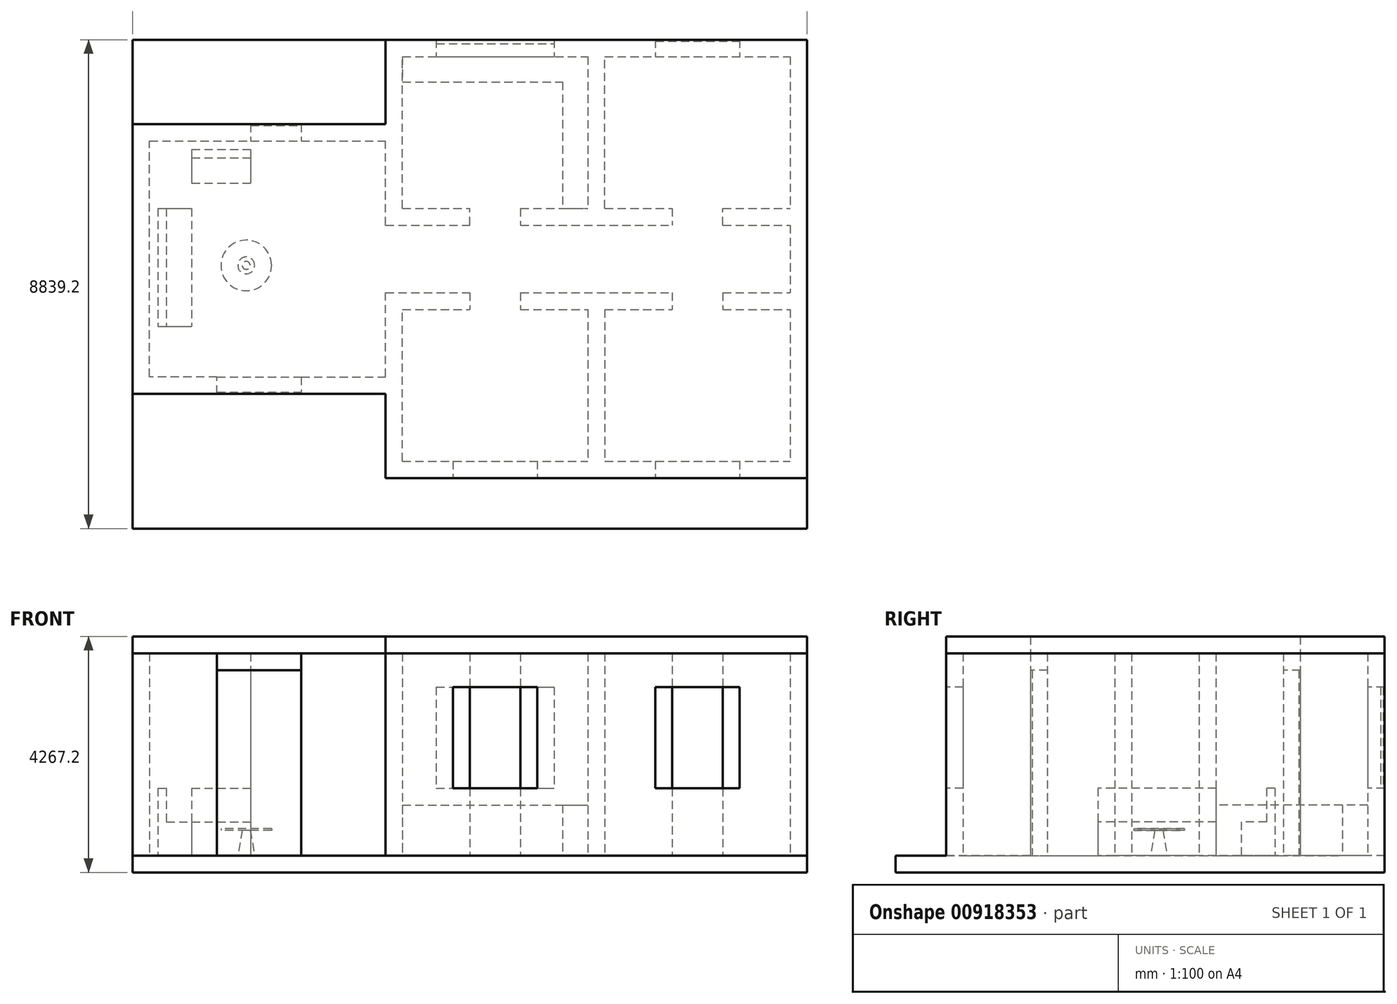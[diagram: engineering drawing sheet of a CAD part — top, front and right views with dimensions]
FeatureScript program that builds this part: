
annotation { "Feature Type Name" : "Feature", "Feature Type Description" : "" }
export const myFeature = defineFeature(function(context is Context, id is Id, definition is map)
    precondition{}
    {
        {
            var Q0;
            Q0=qCreatedBy(makeId("Top.planeOp"),FACE);
            var sketch = newSketch(context, id + "F0", { "sketchPlane" : qUnion([Q0])});
            skLineSegment(sketch, "E0", {"start": v(-1524, -1642.32) * mm, "end": v(0, -1642.32) * mm});
            skLineSegment(sketch, "E1", {"start": v(0, -1642.32) * mm, "end": v(0, -1337.52) * mm});
            skLineSegment(sketch, "E2", {"start": v(0, -1337.52) * mm, "end": v(-1524, -1337.52) * mm});
            skLineSegment(sketch, "E3", {"start": v(-1524, -1337.52) * mm, "end": v(-1524, -1642.32) * mm});
            skLineSegment(sketch, "E4.bottom", {"start": v(1524, -1337.52) * mm, "end": v(3048, -1337.52) * mm});
            skLineSegment(sketch, "E4.top", {"start": v(1524, -1642.32) * mm, "end": v(3048, -1642.32) * mm});
            skLineSegment(sketch, "E4.left", {"start": v(1524, -1337.52) * mm, "end": v(1524, -1642.32) * mm});
            skLineSegment(sketch, "E4.right", {"start": v(3048, -1337.52) * mm, "end": v(3048, -1642.32) * mm});
            skLineSegment(sketch, "E5.bottom", {"start": v(-1524, -1337.52) * mm, "end": v(-1219.2, -1337.52) * mm});
            skLineSegment(sketch, "E5.top", {"start": v(-1524, 3234.48) * mm, "end": v(-1219.2, 3234.48) * mm});
            skLineSegment(sketch, "E5.left", {"start": v(-1524, -1337.52) * mm, "end": v(-1524, 3234.48) * mm});
            skLineSegment(sketch, "E5.right", {"start": v(-1219.2, -1337.52) * mm, "end": v(-1219.2, 3234.48) * mm});
            skLineSegment(sketch, "E6.bottom", {"start": v(-1219.2, 3234.48) * mm, "end": v(609.6, 3234.48) * mm});
            skLineSegment(sketch, "E6.top", {"start": v(-1219.2, 2929.68) * mm, "end": v(609.6, 2929.68) * mm});
            skLineSegment(sketch, "E6.left", {"start": v(-1219.2, 3234.48) * mm, "end": v(-1219.2, 2929.68) * mm});
            skLineSegment(sketch, "E6.right", {"start": v(609.6, 3234.48) * mm, "end": v(609.6, 2929.68) * mm});
            skLineSegment(sketch, "E7.bottom", {"start": v(1524, 3234.48) * mm, "end": v(3048, 3234.48) * mm});
            skLineSegment(sketch, "E7.top", {"start": v(1524, 2929.68) * mm, "end": v(3048, 2929.68) * mm});
            skLineSegment(sketch, "E7.left", {"start": v(1524, 3234.48) * mm, "end": v(1524, 2929.68) * mm});
            skLineSegment(sketch, "E7.right", {"start": v(3048, 3234.48) * mm, "end": v(3048, 2929.68) * mm});
            skLineSegment(sketch, "E8.bottom", {"start": v(3048, -3166.32) * mm, "end": v(3352.8, -3166.32) * mm});
            skLineSegment(sketch, "E8.top", {"start": v(3048, 186.48) * mm, "end": v(3352.8, 186.48) * mm});
            skLineSegment(sketch, "E8.left", {"start": v(3048, -3166.32) * mm, "end": v(3048, 186.48) * mm});
            skLineSegment(sketch, "E8.right", {"start": v(3352.8, -3166.32) * mm, "end": v(3352.8, 186.48) * mm});
            skLineSegment(sketch, "E9.bottom", {"start": v(3352.8, 1405.68) * mm, "end": v(3048, 1405.68) * mm});
            skLineSegment(sketch, "E9.top", {"start": v(3352.8, 4758.48) * mm, "end": v(3048, 4758.48) * mm});
            skLineSegment(sketch, "E9.left", {"start": v(3352.8, 1405.68) * mm, "end": v(3352.8, 4758.48) * mm});
            skLineSegment(sketch, "E9.right", {"start": v(3048, 1405.68) * mm, "end": v(3048, 4758.48) * mm});
            skLineSegment(sketch, "E10.bottom", {"start": v(3352.8, 1405.68) * mm, "end": v(4572, 1405.68) * mm});
            skLineSegment(sketch, "E10.top", {"start": v(3352.8, 1710.48) * mm, "end": v(4572, 1710.48) * mm});
            skLineSegment(sketch, "E10.left", {"start": v(3352.8, 1405.68) * mm, "end": v(3352.8, 1710.48) * mm});
            skLineSegment(sketch, "E10.right", {"start": v(4572, 1405.68) * mm, "end": v(4572, 1710.48) * mm});
            skLineSegment(sketch, "E11.bottom", {"start": v(5486.4, 1710.48) * mm, "end": v(6705.6, 1710.48) * mm});
            skLineSegment(sketch, "E11.top", {"start": v(5486.4, 1405.68) * mm, "end": v(6705.6, 1405.68) * mm});
            skLineSegment(sketch, "E11.left", {"start": v(5486.4, 1710.48) * mm, "end": v(5486.4, 1405.68) * mm});
            skLineSegment(sketch, "E11.right", {"start": v(6705.6, 1710.48) * mm, "end": v(6705.6, 1405.68) * mm});
            skLineSegment(sketch, "E12.bottom", {"start": v(6705.6, 1405.68) * mm, "end": v(7010.4, 1405.68) * mm});
            skLineSegment(sketch, "E12.top", {"start": v(6705.6, 4758.48) * mm, "end": v(7010.4, 4758.48) * mm});
            skLineSegment(sketch, "E12.left", {"start": v(6705.6, 1405.68) * mm, "end": v(6705.6, 4758.48) * mm});
            skLineSegment(sketch, "E12.right", {"start": v(7010.4, 1405.68) * mm, "end": v(7010.4, 4758.48) * mm});
            skLineSegment(sketch, "E13.bottom", {"start": v(3352.8, 4758.48) * mm, "end": v(3962.4, 4758.48) * mm});
            skLineSegment(sketch, "E13.top", {"start": v(3352.8, 4453.68) * mm, "end": v(3962.4, 4453.68) * mm});
            skLineSegment(sketch, "E13.left", {"start": v(3352.8, 4758.48) * mm, "end": v(3352.8, 4453.68) * mm});
            skLineSegment(sketch, "E13.right", {"start": v(3962.4, 4758.48) * mm, "end": v(3962.4, 4453.68) * mm});
            skLineSegment(sketch, "E14.bottom", {"start": v(6096, 4758.48) * mm, "end": v(6705.6, 4758.48) * mm});
            skLineSegment(sketch, "E14.top", {"start": v(6096, 4453.68) * mm, "end": v(6705.6, 4453.68) * mm});
            skLineSegment(sketch, "E14.left", {"start": v(6096, 4758.48) * mm, "end": v(6096, 4453.68) * mm});
            skLineSegment(sketch, "E14.right", {"start": v(6705.6, 4758.48) * mm, "end": v(6705.6, 4453.68) * mm});
            skLineSegment(sketch, "E15.bottom", {"start": v(3352.8, 186.48) * mm, "end": v(4572, 186.48) * mm});
            skLineSegment(sketch, "E15.top", {"start": v(3352.8, -118.32) * mm, "end": v(4572, -118.32) * mm});
            skLineSegment(sketch, "E15.left", {"start": v(3352.8, 186.48) * mm, "end": v(3352.8, -118.32) * mm});
            skLineSegment(sketch, "E15.right", {"start": v(4572, 186.48) * mm, "end": v(4572, -118.32) * mm});
            skLineSegment(sketch, "E16.bottom", {"start": v(5486.4, 186.48) * mm, "end": v(6705.6, 186.48) * mm});
            skLineSegment(sketch, "E16.top", {"start": v(5486.4, -118.32) * mm, "end": v(6705.6, -118.32) * mm});
            skLineSegment(sketch, "E16.left", {"start": v(5486.4, 186.48) * mm, "end": v(5486.4, -118.32) * mm});
            skLineSegment(sketch, "E16.right", {"start": v(6705.6, 186.48) * mm, "end": v(6705.6, -118.32) * mm});
            skLineSegment(sketch, "E17.bottom", {"start": v(6705.6, 186.48) * mm, "end": v(7010.4, 186.48) * mm});
            skLineSegment(sketch, "E17.top", {"start": v(6705.6, -3166.32) * mm, "end": v(7010.4, -3166.32) * mm});
            skLineSegment(sketch, "E17.left", {"start": v(6705.6, 186.48) * mm, "end": v(6705.6, -3166.32) * mm});
            skLineSegment(sketch, "E17.right", {"start": v(7010.4, 186.48) * mm, "end": v(7010.4, -3166.32) * mm});
            skLineSegment(sketch, "E18.left", {"start": v(3352.8, -3166.32) * mm, "end": v(3352.8, -2861.52) * mm});
            skLineSegment(sketch, "E19.left", {"start": v(6705.6, -3166.32) * mm, "end": v(6705.6, -2861.52) * mm});
            skLineSegment(sketch, "E20.bottom", {"start": v(7010.4, 4758.48) * mm, "end": v(7924.8, 4758.48) * mm});
            skLineSegment(sketch, "E20.top", {"start": v(7010.4, 4453.68) * mm, "end": v(7924.8, 4453.68) * mm});
            skLineSegment(sketch, "E20.left", {"start": v(7010.4, 4758.48) * mm, "end": v(7010.4, 4453.68) * mm});
            skLineSegment(sketch, "E20.right", {"start": v(7924.8, 4758.48) * mm, "end": v(7924.8, 4453.68) * mm});
            skLineSegment(sketch, "E21.bottom", {"start": v(9448.8, 4758.48) * mm, "end": v(10363.2, 4758.48) * mm});
            skLineSegment(sketch, "E21.top", {"start": v(9448.8, 4453.68) * mm, "end": v(10363.2, 4453.68) * mm});
            skLineSegment(sketch, "E21.left", {"start": v(9448.8, 4758.48) * mm, "end": v(9448.8, 4453.68) * mm});
            skLineSegment(sketch, "E21.right", {"start": v(10363.2, 4758.48) * mm, "end": v(10363.2, 4453.68) * mm});
            skLineSegment(sketch, "E22.bottom", {"start": v(10363.2, 4758.48) * mm, "end": v(10668, 4758.48) * mm});
            skLineSegment(sketch, "E22.top", {"start": v(10363.2, 1405.68) * mm, "end": v(10668, 1405.68) * mm});
            skLineSegment(sketch, "E22.left", {"start": v(10363.2, 4758.48) * mm, "end": v(10363.2, 1405.68) * mm});
            skLineSegment(sketch, "E22.right", {"start": v(10668, 4758.48) * mm, "end": v(10668, 1405.68) * mm});
            skPoint(sketch, "E23.oppositeSnap0", {"position": v(6858, 1405.68) * mm});
            skLineSegment(sketch, "E23.bottom", {"start": v(7010.4, 1710.48) * mm, "end": v(8229.6, 1710.48) * mm});
            skLineSegment(sketch, "E23.top", {"start": v(7010.4, 1405.68) * mm, "end": v(8229.6, 1405.68) * mm});
            skLineSegment(sketch, "E23.left", {"start": v(7010.4, 1710.48) * mm, "end": v(7010.4, 1405.68) * mm});
            skLineSegment(sketch, "E23.right", {"start": v(8229.6, 1710.48) * mm, "end": v(8229.6, 1405.68) * mm});
            skLineSegment(sketch, "E24.bottom", {"start": v(9144, 1405.68) * mm, "end": v(10363.2, 1405.68) * mm});
            skLineSegment(sketch, "E24.top", {"start": v(9144, 1710.48) * mm, "end": v(10363.2, 1710.48) * mm});
            skLineSegment(sketch, "E24.left", {"start": v(9144, 1405.68) * mm, "end": v(9144, 1710.48) * mm});
            skLineSegment(sketch, "E24.right", {"start": v(10363.2, 1405.68) * mm, "end": v(10363.2, 1710.48) * mm});
            skLineSegment(sketch, "E25.bottom", {"start": v(7010.4, 186.48) * mm, "end": v(8229.6, 186.48) * mm});
            skLineSegment(sketch, "E25.top", {"start": v(7010.4, -118.32) * mm, "end": v(8229.6, -118.32) * mm});
            skLineSegment(sketch, "E25.left", {"start": v(7010.4, 186.48) * mm, "end": v(7010.4, -118.32) * mm});
            skLineSegment(sketch, "E25.right", {"start": v(8229.6, 186.48) * mm, "end": v(8229.6, -118.32) * mm});
            skLineSegment(sketch, "E26.bottom", {"start": v(9144, 186.48) * mm, "end": v(10363.2, 186.48) * mm});
            skLineSegment(sketch, "E26.top", {"start": v(9144, -118.32) * mm, "end": v(10363.2, -118.32) * mm});
            skLineSegment(sketch, "E26.left", {"start": v(9144, 186.48) * mm, "end": v(9144, -118.32) * mm});
            skLineSegment(sketch, "E26.right", {"start": v(10363.2, 186.48) * mm, "end": v(10363.2, -118.32) * mm});
            skLineSegment(sketch, "E27.bottom", {"start": v(7010.4, -3166.32) * mm, "end": v(7924.8, -3166.32) * mm});
            skLineSegment(sketch, "E27.top", {"start": v(7010.4, -2861.52) * mm, "end": v(7924.8, -2861.52) * mm});
            skLineSegment(sketch, "E27.left", {"start": v(7010.4, -3166.32) * mm, "end": v(7010.4, -2861.52) * mm});
            skLineSegment(sketch, "E27.right", {"start": v(7924.8, -3166.32) * mm, "end": v(7924.8, -2861.52) * mm});
            skLineSegment(sketch, "E28.bottom", {"start": v(9448.8, -2861.52) * mm, "end": v(10363.2, -2861.52) * mm});
            skLineSegment(sketch, "E28.top", {"start": v(9448.8, -3166.32) * mm, "end": v(10363.2, -3166.32) * mm});
            skLineSegment(sketch, "E28.left", {"start": v(9448.8, -2861.52) * mm, "end": v(9448.8, -3166.32) * mm});
            skLineSegment(sketch, "E28.right", {"start": v(10363.2, -2861.52) * mm, "end": v(10363.2, -3166.32) * mm});
            skLineSegment(sketch, "E29.top", {"start": v(10363.2, -3166.32) * mm, "end": v(10668, -3166.32) * mm});
            skLineSegment(sketch, "E29.left", {"start": v(10363.2, 1405.68) * mm, "end": v(10363.2, -3166.32) * mm});
            skLineSegment(sketch, "E29.right", {"start": v(10668, 1405.68) * mm, "end": v(10668, -3166.32) * mm});
            skLineSegment(sketch, "E30.bottom", {"start": v(3352.8, -2861.52) * mm, "end": v(4267.2, -2861.52) * mm});
            skLineSegment(sketch, "E30.top", {"start": v(3352.8, -3166.32) * mm, "end": v(4267.2, -3166.32) * mm});
            skLineSegment(sketch, "E30.left", {"start": v(3352.8, -2861.52) * mm, "end": v(3352.8, -3166.32) * mm});
            skLineSegment(sketch, "E30.right", {"start": v(4267.2, -2861.52) * mm, "end": v(4267.2, -3166.32) * mm});
            skLineSegment(sketch, "E31.bottom", {"start": v(6705.6, -2861.52) * mm, "end": v(5791.2, -2861.52) * mm});
            skLineSegment(sketch, "E31.top", {"start": v(6705.6, -3166.32) * mm, "end": v(5791.2, -3166.32) * mm});
            skLineSegment(sketch, "E31.left", {"start": v(6705.6, -2861.52) * mm, "end": v(6705.6, -3166.32) * mm});
            skLineSegment(sketch, "E31.right", {"start": v(5791.2, -2861.52) * mm, "end": v(5791.2, -3166.32) * mm});
            skSolve(sketch);
        }
        {
            var Q0;
            Q0=qSketchRegion(id+"F0",true);
            extrude(context, id + "F1", {"entities" : qUnion([Q0]), "depth" : 3657.6 * mm});
        }
        {
            var Q0;
            Q0=qCreatedBy(makeId("Top.planeOp"),FACE);
            var sketch = newSketch(context, id + "F2", { "sketchPlane" : qUnion([Q0])});
            skLineSegment(sketch, "E32.bottom", {"start": v(-1524, 4758.48) * mm, "end": v(10668, 4758.48) * mm});
            skLineSegment(sketch, "E32.top", {"start": v(-1524, -3166.32) * mm, "end": v(10668, -3166.32) * mm});
            skLineSegment(sketch, "E32.left", {"start": v(-1524, 4758.48) * mm, "end": v(-1524, -3166.32) * mm});
            skLineSegment(sketch, "E32.right", {"start": v(10668, 4758.48) * mm, "end": v(10668, -3166.32) * mm});
            skLineSegment(sketch, "E33.top", {"start": v(-1524, -4080.72) * mm, "end": v(10668, -4080.72) * mm});
            skLineSegment(sketch, "E33.left", {"start": v(-1524, -3166.32) * mm, "end": v(-1524, -4080.72) * mm});
            skLineSegment(sketch, "E33.right", {"start": v(10668, -3166.32) * mm, "end": v(10668, -4080.72) * mm});
            skSolve(sketch);
        }
        {
            var Q0;
            Q0=qSketchRegion(id+"F2",true);
            extrude(context, id + "F3", {"entities" : qUnion([Q0]), "oppositeDirection" : true, "depth" : 304.8 * mm});
        }
        {
            var Q0;
            Q0=qCreatedBy(makeId("Top.planeOp"),FACE);
            var sketch = newSketch(context, id + "F4", { "sketchPlane" : qUnion([Q0])});
            skLineSegment(sketch, "E34.bottom", {"start": v(3962.4, 4758.48) * mm, "end": v(6096, 4758.48) * mm});
            skLineSegment(sketch, "E34.top", {"start": v(3962.4, 4453.68) * mm, "end": v(6096, 4453.68) * mm});
            skLineSegment(sketch, "E34.left", {"start": v(3962.4, 4758.48) * mm, "end": v(3962.4, 4453.68) * mm});
            skLineSegment(sketch, "E34.right", {"start": v(6096, 4758.48) * mm, "end": v(6096, 4453.68) * mm});
            skLineSegment(sketch, "E35.bottom", {"start": v(7924.8, -2861.52) * mm, "end": v(9448.8, -2861.52) * mm});
            skLineSegment(sketch, "E35.top", {"start": v(7924.8, -3166.32) * mm, "end": v(9448.8, -3166.32) * mm});
            skLineSegment(sketch, "E35.left", {"start": v(7924.8, -2861.52) * mm, "end": v(7924.8, -3166.32) * mm});
            skLineSegment(sketch, "E35.right", {"start": v(9448.8, -2861.52) * mm, "end": v(9448.8, -3166.32) * mm});
            skLineSegment(sketch, "E36.bottom", {"start": v(4267.2, -2861.52) * mm, "end": v(5791.2, -2861.52) * mm});
            skLineSegment(sketch, "E36.top", {"start": v(4267.2, -3166.32) * mm, "end": v(5791.2, -3166.32) * mm});
            skLineSegment(sketch, "E36.left", {"start": v(4267.2, -2861.52) * mm, "end": v(4267.2, -3166.32) * mm});
            skLineSegment(sketch, "E36.right", {"start": v(5791.2, -2861.52) * mm, "end": v(5791.2, -3166.32) * mm});
            skSolve(sketch);
        }
        {
            var Q0;
            Q0=qSketchRegion(id+"F4",true);
            extrude(context, id + "F5", {"entities" : qUnion([Q0]), "depth" : 1219.2 * mm});
        }
        {
            var Q0;
            Q0=qCreatedBy(makeId("Top.planeOp"),FACE);
            cPlane(context, id + "F6", {"entities" : qUnion([Q0]), "cplaneType" : CPlaneType.OFFSET, "offset" : 3048 * mm, "width" : 152.4 * mm, "height" : 152.4 * mm});
        }
        {
            var Q0;
            Q0=qCreatedBy(id+"F6.planeOp",FACE);
            var sketch = newSketch(context, id + "F7", { "sketchPlane" : qUnion([Q0])});
            skLineSegment(sketch, "E37.bottom", {"start": v(3962.4, 4758.48) * mm, "end": v(6096, 4758.48) * mm});
            skLineSegment(sketch, "E37.top", {"start": v(3962.4, 4453.68) * mm, "end": v(6096, 4453.68) * mm});
            skLineSegment(sketch, "E37.left", {"start": v(3962.4, 4758.48) * mm, "end": v(3962.4, 4453.68) * mm});
            skLineSegment(sketch, "E37.right", {"start": v(6096, 4758.48) * mm, "end": v(6096, 4453.68) * mm});
            skLineSegment(sketch, "E38.bottom", {"start": v(7924.8, 4758.48) * mm, "end": v(9448.8, 4758.48) * mm});
            skLineSegment(sketch, "E38.top", {"start": v(7924.8, 4453.68) * mm, "end": v(9448.8, 4453.68) * mm});
            skLineSegment(sketch, "E38.left", {"start": v(7924.8, 4758.48) * mm, "end": v(7924.8, 4453.68) * mm});
            skLineSegment(sketch, "E38.right", {"start": v(9448.8, 4758.48) * mm, "end": v(9448.8, 4453.68) * mm});
            skLineSegment(sketch, "E39.bottom", {"start": v(7924.8, -2861.52) * mm, "end": v(9448.8, -2861.52) * mm});
            skLineSegment(sketch, "E39.top", {"start": v(7924.8, -3166.32) * mm, "end": v(9448.8, -3166.32) * mm});
            skLineSegment(sketch, "E39.left", {"start": v(7924.8, -2861.52) * mm, "end": v(7924.8, -3166.32) * mm});
            skLineSegment(sketch, "E39.right", {"start": v(9448.8, -2861.52) * mm, "end": v(9448.8, -3166.32) * mm});
            skLineSegment(sketch, "E40.bottom", {"start": v(4267.2, -2861.52) * mm, "end": v(5791.2, -2861.52) * mm});
            skLineSegment(sketch, "E40.top", {"start": v(4267.2, -3166.32) * mm, "end": v(5791.2, -3166.32) * mm});
            skLineSegment(sketch, "E40.left", {"start": v(4267.2, -2861.52) * mm, "end": v(4267.2, -3166.32) * mm});
            skLineSegment(sketch, "E40.right", {"start": v(5791.2, -2861.52) * mm, "end": v(5791.2, -3166.32) * mm});
            skSolve(sketch);
        }
        {
            var Q0;
            Q0=qSketchRegion(id+"F7",true);
            var Q1;
            Q1=makeQuery(id+"F1.opExtrude","CAP_FACE",FACE,{"disambiguationData":[OSD([sQuery(id+"F0.wireOp",EDGE,"E4.bottom"),sQuery(id+"F0.wireOp",EDGE,"E4.top"),sQuery(id+"F0.wireOp",EDGE,"E4.left"),sQuery(id+"F0.wireOp",EDGE,"E8.bottom"),sQuery(id+"F0.wireOp",EDGE,"E8.top"),sQuery(id+"F0.wireOp",EDGE,"E8.left"),sQuery(id+"F0.wireOp",EDGE,"E8.right"),sQuery(id+"F0.wireOp",EDGE,"E15.bottom"),sQuery(id+"F0.wireOp",EDGE,"E15.top"),sQuery(id+"F0.wireOp",EDGE,"E15.right"),sQuery(id+"F0.wireOp",EDGE,"E18.bottom"),sQuery(id+"F0.wireOp",EDGE,"E18.top"),sQuery(id+"F0.wireOp",EDGE,"E18.right")])],"isStart":false});
            extrude(context, id + "F8", {"entities" : qUnion([Q0]), "depth" : 609.6 * mm});
        }
        {
            var Q0;
            Q0=qCreatedBy(makeId("Top.planeOp"),FACE);
            cPlane(context, id + "F9", {"entities" : qUnion([Q0]), "cplaneType" : CPlaneType.OFFSET, "offset" : 3657.6 * mm, "width" : 152.4 * mm, "height" : 152.4 * mm});
        }
        {
            var Q0;
            Q0=qCreatedBy(id+"F9.planeOp",FACE);
            var sketch = newSketch(context, id + "F10", { "sketchPlane" : qUnion([Q0])});
            skLineSegment(sketch, "E41", {"start": v(-1524, 3234.48) * mm, "end": v(-1524, -1642.32) * mm});
            skLineSegment(sketch, "E42", {"start": v(-1524, -1642.32) * mm, "end": v(3048, -1642.32) * mm});
            skLineSegment(sketch, "E43", {"start": v(3048, -1642.32) * mm, "end": v(3048, -3166.32) * mm});
            skLineSegment(sketch, "E44", {"start": v(3048, -3166.32) * mm, "end": v(10668, -3166.32) * mm});
            skLineSegment(sketch, "E45", {"start": v(10668, -3166.32) * mm, "end": v(10668, 4758.48) * mm});
            skLineSegment(sketch, "E46", {"start": v(10668, 4758.48) * mm, "end": v(3048, 4758.48) * mm});
            skLineSegment(sketch, "E47", {"start": v(3048, 4758.48) * mm, "end": v(3048, 3234.48) * mm});
            skLineSegment(sketch, "E48", {"start": v(3048, 3234.48) * mm, "end": v(-1524, 3234.48) * mm});
            skSolve(sketch);
        }
        {
            var Q0;
            Q0=qSketchRegion(id+"F10",true);
            extrude(context, id + "F11", {"entities" : qUnion([Q0]), "depth" : 304.8 * mm});
        }
        {
            var Q0;
            Q0=makeQuery(id+"F1.opExtrude","SWEPT_BODY",BODY,{"disambiguationData":[OSD([sQuery(id+"F0.wireOp",EDGE,"E0"),sQuery(id+"F0.wireOp",EDGE,"E1"),sQuery(id+"F0.wireOp",EDGE,"E2"),sQuery(id+"F0.wireOp",EDGE,"E3"),sQuery(id+"F0.wireOp",EDGE,"E5.top"),sQuery(id+"F0.wireOp",EDGE,"E5.left"),sQuery(id+"F0.wireOp",EDGE,"E5.right"),sQuery(id+"F0.wireOp",EDGE,"E6.bottom"),sQuery(id+"F0.wireOp",EDGE,"E6.top"),sQuery(id+"F0.wireOp",EDGE,"E6.right")])]});
            var Q1;
            Q1=makeQuery(id+"F1.opExtrude","SWEPT_BODY",BODY,{"disambiguationData":[OSD([sQuery(id+"F0.wireOp",EDGE,"E4.bottom"),sQuery(id+"F0.wireOp",EDGE,"E4.top"),sQuery(id+"F0.wireOp",EDGE,"E4.left"),sQuery(id+"F0.wireOp",EDGE,"E8.bottom"),sQuery(id+"F0.wireOp",EDGE,"E8.top"),sQuery(id+"F0.wireOp",EDGE,"E8.left"),sQuery(id+"F0.wireOp",EDGE,"E8.right"),sQuery(id+"F0.wireOp",EDGE,"E15.bottom"),sQuery(id+"F0.wireOp",EDGE,"E15.top"),sQuery(id+"F0.wireOp",EDGE,"E15.right"),sQuery(id+"F0.wireOp",EDGE,"E18.bottom"),sQuery(id+"F0.wireOp",EDGE,"E18.top"),sQuery(id+"F0.wireOp",EDGE,"E18.right")])]});
            var Q2;
            Q2=makeQuery(id+"F1.opExtrude","SWEPT_BODY",BODY,{"disambiguationData":[OSD([sQuery(id+"F0.wireOp",EDGE,"E7.bottom"),sQuery(id+"F0.wireOp",EDGE,"E7.top"),sQuery(id+"F0.wireOp",EDGE,"E7.left"),sQuery(id+"F0.wireOp",EDGE,"E9.bottom"),sQuery(id+"F0.wireOp",EDGE,"E9.top"),sQuery(id+"F0.wireOp",EDGE,"E9.left"),sQuery(id+"F0.wireOp",EDGE,"E9.right"),sQuery(id+"F0.wireOp",EDGE,"E10.bottom"),sQuery(id+"F0.wireOp",EDGE,"E10.top"),sQuery(id+"F0.wireOp",EDGE,"E10.right"),sQuery(id+"F0.wireOp",EDGE,"E13.bottom"),sQuery(id+"F0.wireOp",EDGE,"E13.top"),sQuery(id+"F0.wireOp",EDGE,"E13.right")])]});
            var Q3;
            Q3=makeQuery(id+"F1.opExtrude","SWEPT_BODY",BODY,{"disambiguationData":[OSD([sQuery(id+"F0.wireOp",EDGE,"E11.bottom"),sQuery(id+"F0.wireOp",EDGE,"E11.top"),sQuery(id+"F0.wireOp",EDGE,"E11.left"),sQuery(id+"F0.wireOp",EDGE,"E12.bottom"),sQuery(id+"F0.wireOp",EDGE,"E12.top"),sQuery(id+"F0.wireOp",EDGE,"E12.left"),sQuery(id+"F0.wireOp",EDGE,"E12.right"),sQuery(id+"F0.wireOp",EDGE,"E14.bottom"),sQuery(id+"F0.wireOp",EDGE,"E14.top"),sQuery(id+"F0.wireOp",EDGE,"E14.left"),sQuery(id+"F0.wireOp",EDGE,"E20.bottom"),sQuery(id+"F0.wireOp",EDGE,"E20.top"),sQuery(id+"F0.wireOp",EDGE,"E20.right"),sQuery(id+"F0.wireOp",EDGE,"E23.bottom"),sQuery(id+"F0.wireOp",EDGE,"E23.top"),sQuery(id+"F0.wireOp",EDGE,"E23.right")])]});
            var Q4;
            Q4=makeQuery(id+"F1.opExtrude","SWEPT_BODY",BODY,{"disambiguationData":[OSD([sQuery(id+"F0.wireOp",EDGE,"E16.bottom"),sQuery(id+"F0.wireOp",EDGE,"E16.top"),sQuery(id+"F0.wireOp",EDGE,"E16.left"),sQuery(id+"F0.wireOp",EDGE,"E17.bottom"),sQuery(id+"F0.wireOp",EDGE,"E17.top"),sQuery(id+"F0.wireOp",EDGE,"E17.left"),sQuery(id+"F0.wireOp",EDGE,"E17.right"),sQuery(id+"F0.wireOp",EDGE,"E19.bottom"),sQuery(id+"F0.wireOp",EDGE,"E19.top"),sQuery(id+"F0.wireOp",EDGE,"E19.right"),sQuery(id+"F0.wireOp",EDGE,"E25.bottom"),sQuery(id+"F0.wireOp",EDGE,"E25.top"),sQuery(id+"F0.wireOp",EDGE,"E25.right"),sQuery(id+"F0.wireOp",EDGE,"E27.bottom"),sQuery(id+"F0.wireOp",EDGE,"E27.top"),sQuery(id+"F0.wireOp",EDGE,"E27.right")])]});
            var Q5;
            Q5=makeQuery(id+"F1.opExtrude","SWEPT_BODY",BODY,{"disambiguationData":[OSD([sQuery(id+"F0.wireOp",EDGE,"E21.bottom"),sQuery(id+"F0.wireOp",EDGE,"E21.top"),sQuery(id+"F0.wireOp",EDGE,"E21.left"),sQuery(id+"F0.wireOp",EDGE,"E22.bottom"),sQuery(id+"F0.wireOp",EDGE,"E22.top"),sQuery(id+"F0.wireOp",EDGE,"E22.left"),sQuery(id+"F0.wireOp",EDGE,"E22.right"),sQuery(id+"F0.wireOp",EDGE,"E24.bottom"),sQuery(id+"F0.wireOp",EDGE,"E24.top"),sQuery(id+"F0.wireOp",EDGE,"E24.left")])]});
            var Q6;
            Q6=makeQuery(id+"F1.opExtrude","SWEPT_BODY",BODY,{"disambiguationData":[OSD([sQuery(id+"F0.wireOp",EDGE,"E26.bottom"),sQuery(id+"F0.wireOp",EDGE,"E26.top"),sQuery(id+"F0.wireOp",EDGE,"E26.left"),sQuery(id+"F0.wireOp",EDGE,"E26.right")])]});
            var Q7;
            Q7=makeQuery(id+"F1.opExtrude","SWEPT_BODY",BODY,{"disambiguationData":[OSD([sQuery(id+"F0.wireOp",EDGE,"E28.bottom"),sQuery(id+"F0.wireOp",EDGE,"E28.top"),sQuery(id+"F0.wireOp",EDGE,"E28.left"),sQuery(id+"F0.wireOp",EDGE,"E28.right")])]});
            var Q8;
            Q8=makeQuery(id+"F1.opExtrude","SWEPT_BODY",BODY,{"disambiguationData":[OSD([sQuery(id+"F0.wireOp",EDGE,"E22.top"),sQuery(id+"F0.wireOp",EDGE,"E29.top"),sQuery(id+"F0.wireOp",EDGE,"E29.left"),sQuery(id+"F0.wireOp",EDGE,"E29.right")])]});
            var Q9;
            Q9=makeQuery(id+"F3.opExtrude","SWEPT_BODY",BODY,{"disambiguationData":[OSD([sQuery(id+"F2.wireOp",EDGE,"E32.bottom"),sQuery(id+"F2.wireOp",EDGE,"E32.top"),sQuery(id+"F2.wireOp",EDGE,"E32.left"),sQuery(id+"F2.wireOp",EDGE,"E32.right")])]});
            var Q10;
            Q10=makeQuery(id+"F5.opExtrude","SWEPT_BODY",BODY,{"disambiguationData":[OSD([sQuery(id+"F4.wireOp",EDGE,"E34.bottom"),sQuery(id+"F4.wireOp",EDGE,"E34.top"),sQuery(id+"F4.wireOp",EDGE,"E34.left"),sQuery(id+"F4.wireOp",EDGE,"E34.right")])]});
            var Q11;
            Q11=makeQuery(id+"F5.opExtrude","SWEPT_BODY",BODY,{"disambiguationData":[OSD([sQuery(id+"F4.wireOp",EDGE,"46e9026d-46fc-4155-8c71-2280dcd3004d.bottom"),sQuery(id+"F4.wireOp",EDGE,"46e9026d-46fc-4155-8c71-2280dcd3004d.top"),sQuery(id+"F4.wireOp",EDGE,"46e9026d-46fc-4155-8c71-2280dcd3004d.left"),sQuery(id+"F4.wireOp",EDGE,"46e9026d-46fc-4155-8c71-2280dcd3004d.right")])]});
            var Q12;
            Q12=makeQuery(id+"F5.opExtrude","SWEPT_BODY",BODY,{"disambiguationData":[OSD([sQuery(id+"F4.wireOp",EDGE,"E35.bottom"),sQuery(id+"F4.wireOp",EDGE,"E35.top"),sQuery(id+"F4.wireOp",EDGE,"E35.left"),sQuery(id+"F4.wireOp",EDGE,"E35.right")])]});
            var Q13;
            Q13=makeQuery(id+"F5.opExtrude","SWEPT_BODY",BODY,{"disambiguationData":[OSD([sQuery(id+"F4.wireOp",EDGE,"E36.bottom"),sQuery(id+"F4.wireOp",EDGE,"E36.top"),sQuery(id+"F4.wireOp",EDGE,"E36.left"),sQuery(id+"F4.wireOp",EDGE,"E36.right")])]});
            var Q14;
            Q14=makeQuery(id+"F8.opExtrude","SWEPT_BODY",BODY,{"disambiguationData":[OSD([sQuery(id+"F7.wireOp",EDGE,"E37.bottom"),sQuery(id+"F7.wireOp",EDGE,"E37.top"),sQuery(id+"F7.wireOp",EDGE,"E37.left"),sQuery(id+"F7.wireOp",EDGE,"E37.right")])]});
            var Q15;
            Q15=makeQuery(id+"F8.opExtrude","SWEPT_BODY",BODY,{"disambiguationData":[OSD([sQuery(id+"F7.wireOp",EDGE,"E38.bottom"),sQuery(id+"F7.wireOp",EDGE,"E38.top"),sQuery(id+"F7.wireOp",EDGE,"E38.left"),sQuery(id+"F7.wireOp",EDGE,"E38.right")])]});
            var Q16;
            Q16=makeQuery(id+"F8.opExtrude","SWEPT_BODY",BODY,{"disambiguationData":[OSD([sQuery(id+"F7.wireOp",EDGE,"E39.bottom"),sQuery(id+"F7.wireOp",EDGE,"E39.top"),sQuery(id+"F7.wireOp",EDGE,"E39.left"),sQuery(id+"F7.wireOp",EDGE,"E39.right")])]});
            var Q17;
            Q17=makeQuery(id+"F8.opExtrude","SWEPT_BODY",BODY,{"disambiguationData":[OSD([sQuery(id+"F7.wireOp",EDGE,"E40.bottom"),sQuery(id+"F7.wireOp",EDGE,"E40.top"),sQuery(id+"F7.wireOp",EDGE,"E40.left"),sQuery(id+"F7.wireOp",EDGE,"E40.right")])]});
            booleanBodies(context, id + "F12", {"operationType" : BooleanOperationType.UNION, "tools" : qUnion([Q0, Q1, Q2, Q3, Q4, Q5, Q6, Q7, Q8, Q9, Q10, Q11, Q12, Q13, Q14, Q15, Q16, Q17])});
        }
        {
            var Q0;
            Q0=qCreatedBy(makeId("Top.planeOp"),FACE);
            var sketch = newSketch(context, id + "F13", { "sketchPlane" : qUnion([Q0])});
            skLineSegment(sketch, "E49.bottom", {"start": v(0, -1642.32) * mm, "end": v(1524, -1642.32) * mm});
            skLineSegment(sketch, "E49.top", {"start": v(0, -1611.84) * mm, "end": v(1524, -1611.84) * mm});
            skLineSegment(sketch, "E49.left", {"start": v(0, -1642.32) * mm, "end": v(0, -1611.84) * mm});
            skLineSegment(sketch, "E49.right", {"start": v(1524, -1642.32) * mm, "end": v(1524, -1611.84) * mm});
            skLineSegment(sketch, "E50.bottom", {"start": v(609.6, 3234.48) * mm, "end": v(1524, 3234.48) * mm});
            skLineSegment(sketch, "E50.top", {"start": v(609.6, 3204) * mm, "end": v(1524, 3204) * mm});
            skLineSegment(sketch, "E50.left", {"start": v(609.6, 3234.48) * mm, "end": v(609.6, 3204) * mm});
            skLineSegment(sketch, "E50.right", {"start": v(1524, 3234.48) * mm, "end": v(1524, 3204) * mm});
            skSolve(sketch);
        }
        {
            var Q0;
            Q0=qSketchRegion(id+"F13",true);
            extrude(context, id + "F14", {"entities" : qUnion([Q0]), "depth" : 3352.8 * mm});
        }
        {
            var Q0;
            Q0=qCreatedBy(makeId("Top.planeOp"),FACE);
            var sketch = newSketch(context, id + "F15", { "sketchPlane" : qUnion([Q0])});
            skLineSegment(sketch, "E51.bottom", {"start": v(7924.8, 4758.48) * mm, "end": v(9448.8, 4758.48) * mm});
            skLineSegment(sketch, "E51.top", {"start": v(7924.8, 4453.68) * mm, "end": v(9448.8, 4453.68) * mm});
            skLineSegment(sketch, "E51.left", {"start": v(7924.8, 4758.48) * mm, "end": v(7924.8, 4453.68) * mm});
            skLineSegment(sketch, "E51.right", {"start": v(9448.8, 4758.48) * mm, "end": v(9448.8, 4453.68) * mm});
            skSolve(sketch);
        }
        {
            var Q0;
            Q0=qSketchRegion(id+"F15",true);
            extrude(context, id + "F16", {"entities" : qUnion([Q0]), "operationType" : NewBodyOperationType.ADD, "depth" : 1219.2 * mm});
        }
        {
            var Q0;
            Q0=qCreatedBy(makeId("Top.planeOp"),FACE);
            var sketch = newSketch(context, id + "F17", { "sketchPlane" : qUnion([Q0])});
            skLineSegment(sketch, "E52.bottom", {"start": v(3352.8, 4453.68) * mm, "end": v(6705.6, 4453.68) * mm});
            skLineSegment(sketch, "E52.top", {"start": v(3352.8, 3996.48) * mm, "end": v(6705.6, 3996.48) * mm});
            skLineSegment(sketch, "E52.left", {"start": v(3352.8, 4453.68) * mm, "end": v(3352.8, 3996.48) * mm});
            skLineSegment(sketch, "E52.right", {"start": v(6705.6, 4453.68) * mm, "end": v(6705.6, 3996.48) * mm});
            skLineSegment(sketch, "E53.bottom", {"start": v(6248.4, 3996.48) * mm, "end": v(6705.6, 3996.48) * mm});
            skLineSegment(sketch, "E53.top", {"start": v(6248.4, 1710.48) * mm, "end": v(6705.6, 1710.48) * mm});
            skLineSegment(sketch, "E53.left", {"start": v(6248.4, 3996.48) * mm, "end": v(6248.4, 1710.48) * mm});
            skLineSegment(sketch, "E53.right", {"start": v(6705.6, 3996.48) * mm, "end": v(6705.6, 1710.48) * mm});
            skSolve(sketch);
        }
        {
            var Q0;
            Q0=qSketchRegion(id+"F17",true);
            extrude(context, id + "F18", {"entities" : qUnion([Q0]), "operationType" : NewBodyOperationType.ADD, "depth" : 914.4 * mm});
        }
        {
            var Q0;
            Q0=qCreatedBy(makeId("Top.planeOp"),FACE);
            var sketch = newSketch(context, id + "F19", { "sketchPlane" : qUnion([Q0])});
            skLineSegment(sketch, "E54.bottom", {"start": v(-457.2, 2777.28) * mm, "end": v(609.6, 2777.28) * mm});
            skLineSegment(sketch, "E54.top", {"start": v(-457.2, 2167.68) * mm, "end": v(609.6, 2167.68) * mm});
            skLineSegment(sketch, "E54.left", {"start": v(-457.2, 2777.28) * mm, "end": v(-457.2, 2167.68) * mm});
            skLineSegment(sketch, "E54.right", {"start": v(609.6, 2777.28) * mm, "end": v(609.6, 2167.68) * mm});
            skLineSegment(sketch, "E55.bottom", {"start": v(-1066.8, 1710.48) * mm, "end": v(-457.2, 1710.48) * mm});
            skLineSegment(sketch, "E55.top", {"start": v(-1066.8, -423.12) * mm, "end": v(-457.2, -423.12) * mm});
            skLineSegment(sketch, "E55.left", {"start": v(-1066.8, 1710.48) * mm, "end": v(-1066.8, -423.12) * mm});
            skLineSegment(sketch, "E55.right", {"start": v(-457.2, 1710.48) * mm, "end": v(-457.2, -423.12) * mm});
            skSolve(sketch);
        }
        {
            var Q0;
            Q0=qSketchRegion(id+"F19",true);
            extrude(context, id + "F20", {"entities" : qUnion([Q0]), "operationType" : NewBodyOperationType.ADD, "depth" : 609.6 * mm});
        }
        {
            var Q0;
            Q0=makeQuery(id+"F20.opExtrude","CAP_FACE",FACE,{"disambiguationData":[OSD([sQuery(id+"F19.wireOp",EDGE,"E54.bottom"),sQuery(id+"F19.wireOp",EDGE,"E54.top"),sQuery(id+"F19.wireOp",EDGE,"E54.left"),sQuery(id+"F19.wireOp",EDGE,"E54.right")])],"isStart":false});
            var sketch = newSketch(context, id + "F21", { "sketchPlane" : qUnion([Q0])});
            skLineSegment(sketch, "E56.bottom", {"start": v(-457.2, 2777.28) * mm, "end": v(609.6, 2777.28) * mm});
            skLineSegment(sketch, "E56.top", {"start": v(-457.2, 2624.88) * mm, "end": v(609.6, 2624.88) * mm});
            skLineSegment(sketch, "E56.left", {"start": v(-457.2, 2777.28) * mm, "end": v(-457.2, 2624.88) * mm});
            skLineSegment(sketch, "E56.right", {"start": v(609.6, 2777.28) * mm, "end": v(609.6, 2624.88) * mm});
            skLineSegment(sketch, "E57.bottom", {"start": v(-1066.8, 1710.48) * mm, "end": v(-914.4, 1710.48) * mm});
            skLineSegment(sketch, "E57.top", {"start": v(-1066.8, -423.12) * mm, "end": v(-914.4, -423.12) * mm});
            skLineSegment(sketch, "E57.left", {"start": v(-1066.8, 1710.48) * mm, "end": v(-1066.8, -423.12) * mm});
            skLineSegment(sketch, "E57.right", {"start": v(-914.4, 1710.48) * mm, "end": v(-914.4, -423.12) * mm});
            skSolve(sketch);
        }
        {
            var Q0;
            Q0=qSketchRegion(id+"F21",true);
            extrude(context, id + "F22", {"entities" : qUnion([Q0]), "operationType" : NewBodyOperationType.ADD, "depth" : 609.6 * mm});
        }
        {
            var Q0;
            Q0=qCreatedBy(makeId("Top.planeOp"),FACE);
            var sketch = newSketch(context, id + "F23", { "sketchPlane" : qUnion([Q0])});
            skCircle(sketch, "E58", {"center": v(527.59, 676.93) * mm, "radius": 152.4 * mm});
            skSolve(sketch);
        }
        {
            var Q0;
            Q0=qSketchRegion(id+"F23",true);
            extrude(context, id + "F24", {"entities" : qUnion([Q0]), "operationType" : NewBodyOperationType.ADD, "depth" : 457.2 * mm, "hasDraft" : true, "draftAngle" : 10 * degree, "draftPullDirection" : true});
        }
        {
            var Q0;
            Q0=makeQuery(id+"F24.opExtrude","CAP_FACE",FACE,{"disambiguationData":[OSD([sQuery(id+"F23.wireOp",EDGE,"E58")])],"isStart":false});
            var sketch = newSketch(context, id + "F25", { "sketchPlane" : qUnion([Q0])});
            skCircle(sketch, "E59", {"center": v(527.59, 676.93) * mm, "radius": 457.2 * mm});
            skSolve(sketch);
        }
        {
            var Q0;
            Q0=qSketchRegion(id+"F25",true);
            extrude(context, id + "F26", {"entities" : qUnion([Q0]), "operationType" : NewBodyOperationType.ADD, "depth" : 30.48 * mm});
        }
        {
            var Q0;
            Q0=makeQuery(id+"F14.opExtrude","CAP_FACE",FACE,{"disambiguationData":[OSD([sQuery(id+"F13.wireOp",EDGE,"E50.bottom"),sQuery(id+"F13.wireOp",EDGE,"E50.top"),sQuery(id+"F13.wireOp",EDGE,"E50.left"),sQuery(id+"F13.wireOp",EDGE,"E50.right")])],"isStart":false});
            var sketch = newSketch(context, id + "F27", { "sketchPlane" : qUnion([Q0])});
            skLineSegment(sketch, "E60.bottom", {"start": v(609.6, 3234.48) * mm, "end": v(1524, 3234.48) * mm});
            skLineSegment(sketch, "E60.top", {"start": v(609.6, 2929.68) * mm, "end": v(1524, 2929.68) * mm});
            skLineSegment(sketch, "E60.left", {"start": v(609.6, 3234.48) * mm, "end": v(609.6, 2929.68) * mm});
            skLineSegment(sketch, "E60.right", {"start": v(1524, 3234.48) * mm, "end": v(1524, 2929.68) * mm});
            skLineSegment(sketch, "E61.bottom", {"start": v(0, -1337.52) * mm, "end": v(1524, -1337.52) * mm});
            skLineSegment(sketch, "E61.top", {"start": v(0, -1642.32) * mm, "end": v(1524, -1642.32) * mm});
            skLineSegment(sketch, "E61.left", {"start": v(0, -1337.52) * mm, "end": v(0, -1642.32) * mm});
            skLineSegment(sketch, "E61.right", {"start": v(1524, -1337.52) * mm, "end": v(1524, -1642.32) * mm});
            skSolve(sketch);
        }
        {
            var Q0;
            Q0=qSketchRegion(id+"F27",true);
            extrude(context, id + "F28", {"entities" : qUnion([Q0]), "depth" : 304.8 * mm});
        }
        {
            var Q0;
            Q0=makeQuery(id+"F16.opExtrude","CAP_FACE",FACE,{"disambiguationData":[OSD([sQuery(id+"F15.wireOp",EDGE,"E51.bottom"),sQuery(id+"F15.wireOp",EDGE,"E51.top"),sQuery(id+"F15.wireOp",EDGE,"E51.left"),sQuery(id+"F15.wireOp",EDGE,"E51.right")])],"isStart":false});
            var sketch = newSketch(context, id + "F29", { "sketchPlane" : qUnion([Q0])});
            skLineSegment(sketch, "E62.bottom", {"start": v(7924.8, 4758.48) * mm, "end": v(9448.8, 4758.48) * mm});
            skLineSegment(sketch, "E62.top", {"start": v(7924.8, 4728) * mm, "end": v(9448.8, 4728) * mm});
            skLineSegment(sketch, "E62.left", {"start": v(7924.8, 4758.48) * mm, "end": v(7924.8, 4728) * mm});
            skLineSegment(sketch, "E62.right", {"start": v(9448.8, 4758.48) * mm, "end": v(9448.8, 4728) * mm});
            skSolve(sketch);
        }
        {
            var Q0;
            Q0=qSketchRegion(id+"F29",true);
            extrude(context, id + "F30", {"entities" : qUnion([Q0]), "depth" : 1828.8 * mm});
        }
        {
            var Q0;
            Q0=makeQuery(id+"F5.opExtrude","CAP_FACE",FACE,{"disambiguationData":[OSD([sQuery(id+"F4.wireOp",EDGE,"E34.bottom"),sQuery(id+"F4.wireOp",EDGE,"E34.top"),sQuery(id+"F4.wireOp",EDGE,"E34.left"),sQuery(id+"F4.wireOp",EDGE,"E34.right")])],"isStart":false});
            var sketch = newSketch(context, id + "F31", { "sketchPlane" : qUnion([Q0])});
            skLineSegment(sketch, "E63.bottom", {"start": v(3962.4, 4758.48) * mm, "end": v(6096, 4758.48) * mm});
            skLineSegment(sketch, "E63.top", {"start": v(3962.4, 4683.97) * mm, "end": v(6096, 4683.97) * mm});
            skLineSegment(sketch, "E63.left", {"start": v(3962.4, 4758.48) * mm, "end": v(3962.4, 4683.97) * mm});
            skLineSegment(sketch, "E63.right", {"start": v(6096, 4758.48) * mm, "end": v(6096, 4683.97) * mm});
            skSolve(sketch);
        }
        {
            var Q0;
            Q0=qSketchRegion(id+"F31",true);
            extrude(context, id + "F32", {"entities" : qUnion([Q0]), "depth" : 1828.8 * mm});
        }
    });
